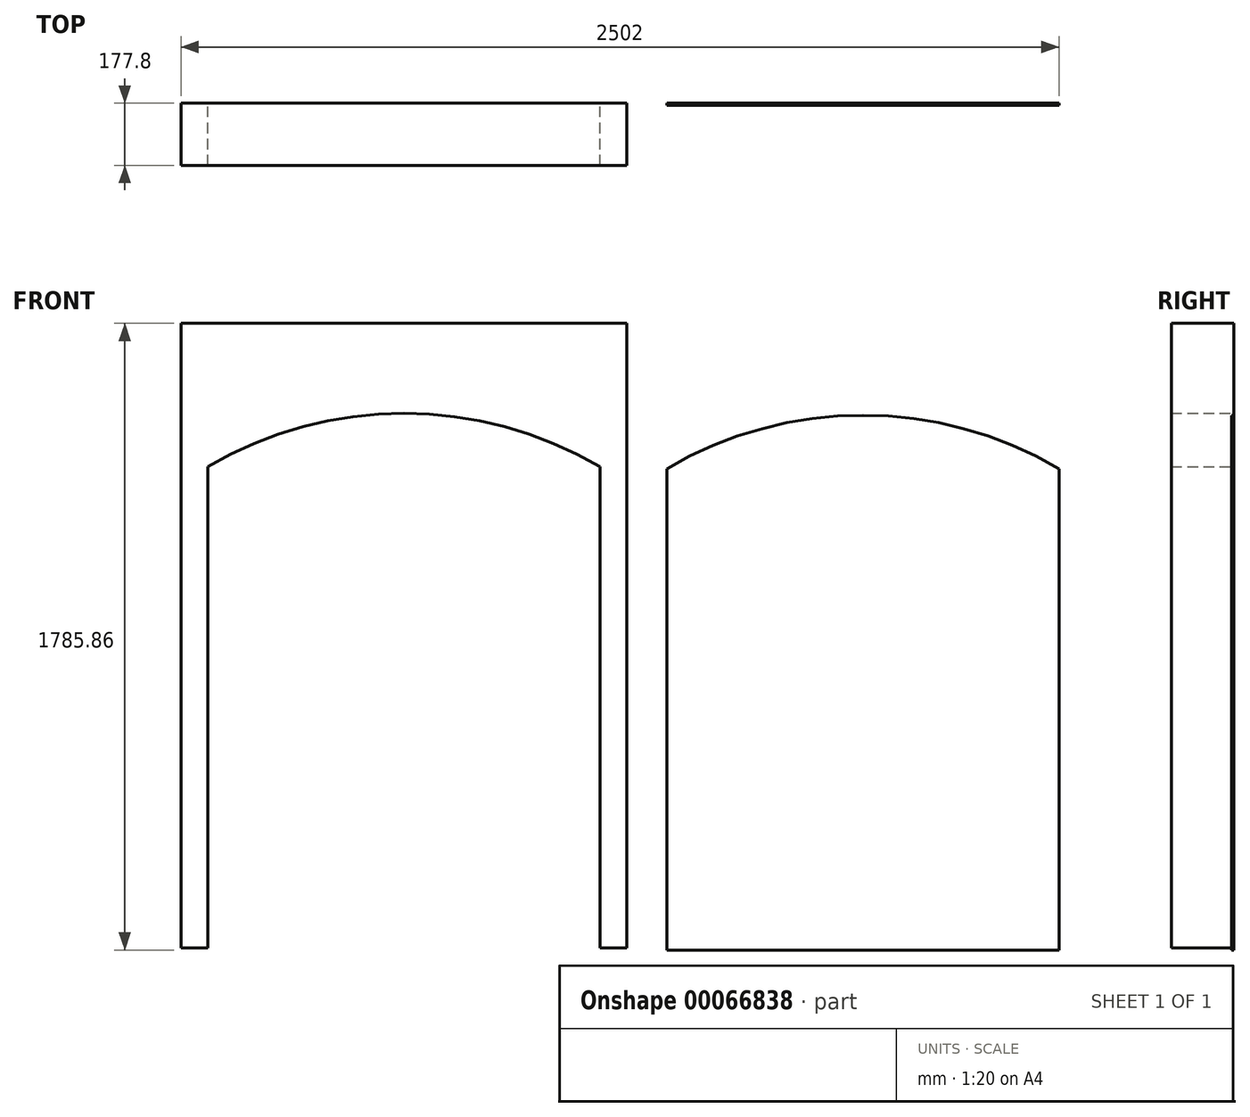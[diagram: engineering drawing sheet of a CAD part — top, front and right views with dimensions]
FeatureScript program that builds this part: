
annotation { "Feature Type Name" : "Feature", "Feature Type Description" : "" }
export const myFeature = defineFeature(function(context is Context, id is Id, definition is map)
    precondition{}
    {
        {
            var Q0;
            Q0=qCreatedBy(makeId("Front.planeOp"),FACE);
            var sketch = newSketch(context, id + "F0", { "sketchPlane" : qUnion([Q0])});
            skLineSegment(sketch, "E0.bottom", {"start": v(-532.17, -879.21) * mm, "end": v(585.43, -879.21) * mm});
            skLineSegment(sketch, "E0.top", {"start": v(-532.17, 492.39) * mm, "end": v(585.43, 492.39) * mm});
            skLineSegment(sketch, "E0.left", {"start": v(-532.17, -879.21) * mm, "end": v(-532.17, 492.39) * mm});
            skLineSegment(sketch, "E0.right", {"start": v(585.43, -879.21) * mm, "end": v(585.43, 492.39) * mm});
            skLineSegment(sketch, "E1.bottom", {"start": v(-608.37, -879.21) * mm, "end": v(661.63, -879.21) * mm});
            skLineSegment(sketch, "E1.top", {"start": v(-608.37, 900.95) * mm, "end": v(661.63, 900.95) * mm});
            skLineSegment(sketch, "E1.left", {"start": v(-608.37, -879.21) * mm, "end": v(-608.37, 900.95) * mm});
            skLineSegment(sketch, "E1.right", {"start": v(661.63, -879.21) * mm, "end": v(661.63, 900.95) * mm});
            skArc(sketch, "E2", {"start": v(585.43, 492.39) * mm, "mid": v(26.63, 644.79) * mm, "end": v(-532.17, 492.39) * mm});
            skSolve(sketch);
        }
        {
            var Q0;
            {var subQ3=sQuery(id+"F0.wireOp",EDGE,"E0.left");Q0=makeQuery(id+"F0.imprint","IMPRINT",FACE,{"disambiguationData":[TD([[makeQuery(id+"F0.imprint","IMPRINT",EDGE,{"derivedFrom":subQ3}),1.0]])]});}
            extrude(context, id + "F1", {"entities" : qUnion([Q0]), "depth" : 177.8 * mm});
        }
        {
            var Q0;
            Q0=makeQuery(id+"F0.imprint","IMPRINT",FACE,{"disambiguationData":[TD([[makeQuery(id+"F0.imprint","IMPRINT",EDGE,{"derivedFrom":sQuery(id+"F0.wireOp",EDGE,"E0.top")}),-1.0]])]});
            var sketch = newSketch(context, id + "F2", { "sketchPlane" : qUnion([Q0])});
            skLineSegment(sketch, "E3.bottom", {"start": v(776.03, -884.91) * mm, "end": v(1893.63, -884.91) * mm});
            skLineSegment(sketch, "E3.top", {"start": v(776.03, 486.69) * mm, "end": v(1893.63, 486.69) * mm});
            skLineSegment(sketch, "E3.left", {"start": v(776.03, -884.91) * mm, "end": v(776.03, 486.69) * mm});
            skLineSegment(sketch, "E3.right", {"start": v(1893.63, -884.91) * mm, "end": v(1893.63, 486.69) * mm});
            skArc(sketch, "E4", {"start": v(1893.63, 486.69) * mm, "mid": v(1334.83, 639.09) * mm, "end": v(776.03, 486.69) * mm});
            skSolve(sketch);
        }
        {
            var Q0;
            Q0=makeQuery(id+"F2.imprint","IMPRINT",FACE,{"disambiguationData":[TD([[makeQuery(id+"F2.imprint","IMPRINT",EDGE,{"derivedFrom":sQuery(id+"F2.wireOp",EDGE,"E3.bottom")}),1.0]])]});
            var Q1;
            Q1=makeQuery(id+"F2.imprint","IMPRINT",FACE,{"disambiguationData":[TD([[makeQuery(id+"F2.imprint","IMPRINT",EDGE,{"derivedFrom":sQuery(id+"F2.wireOp",EDGE,"E3.top")}),1.0]])]});
            extrude(context, id + "F3", {"entities" : qUnion([Q0, Q1]), "depth" : 6.35 * mm});
        }
    });
